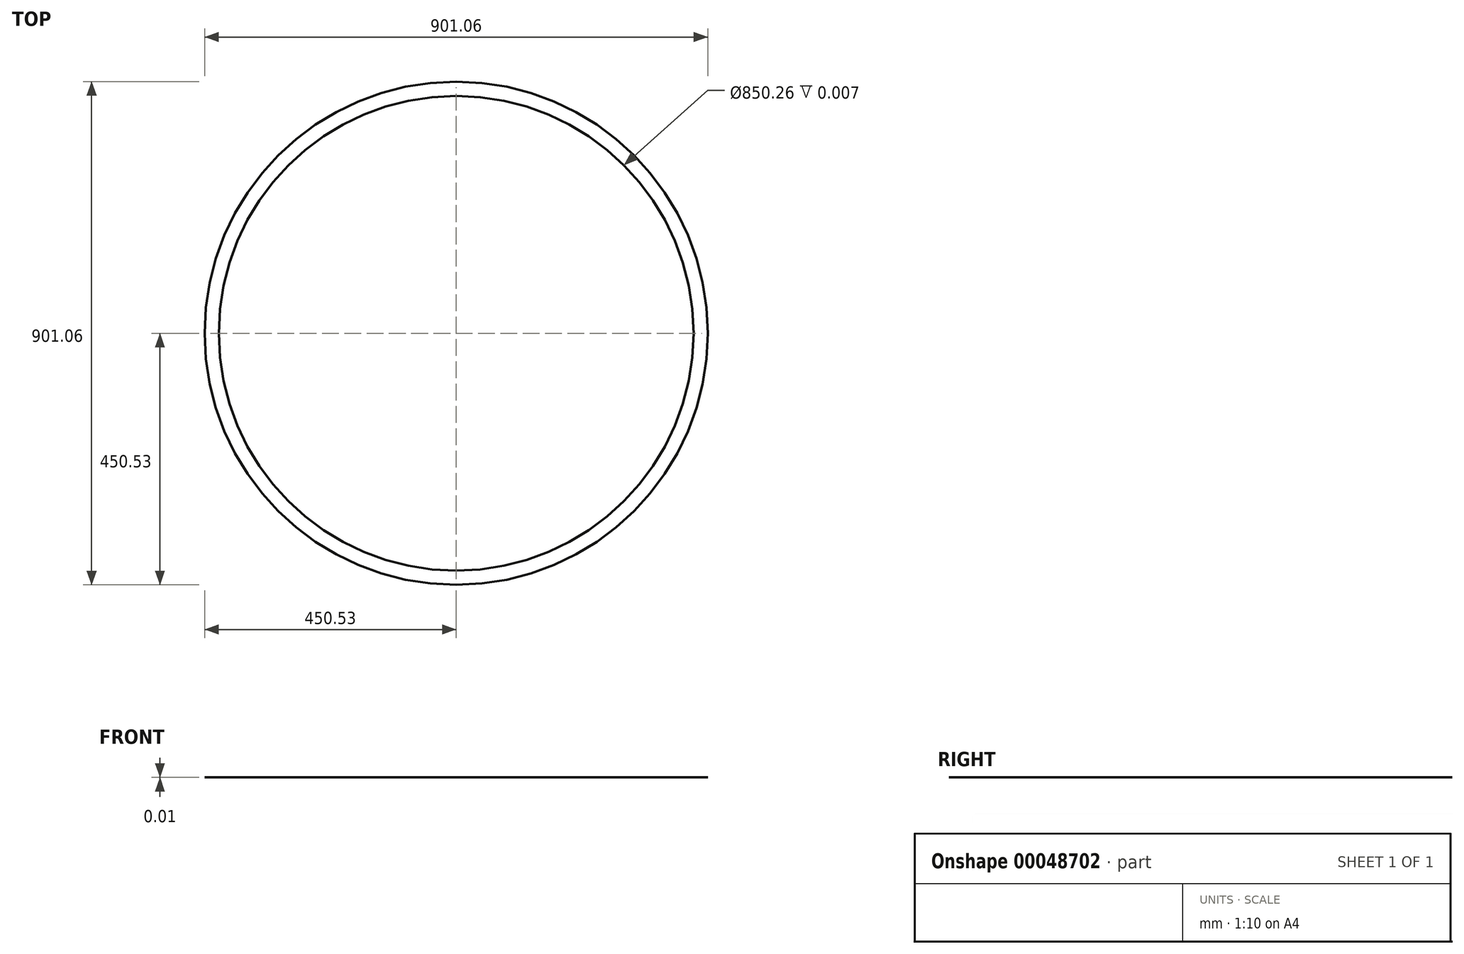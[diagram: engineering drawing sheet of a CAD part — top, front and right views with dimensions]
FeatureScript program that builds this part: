
annotation { "Feature Type Name" : "Feature", "Feature Type Description" : "" }
export const myFeature = defineFeature(function(context is Context, id is Id, definition is map)
    precondition{}
    {
        {
            var Q0;
            Q0=qCreatedBy(makeId("Top.planeOp"),FACE);
            var sketch = newSketch(context, id + "F0", { "sketchPlane" : qUnion([Q0])});
            skCircle(sketch, "E0", {"center": v(0, 0) * mm, "radius": 450.53 * mm});
            skCircle(sketch, "E1", {"center": v(0, 0) * mm, "radius": 425.13 * mm});
            skSolve(sketch);
        }
        {
            var Q0;
            Q0 = qSketchRegion(id + "F0", true);
            extrude(context, id + "F1", {"entities" : qUnion([Q0]), "depth" : 3 / 457.2 * mm});
        }
    });
